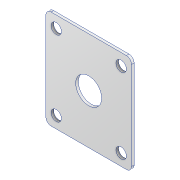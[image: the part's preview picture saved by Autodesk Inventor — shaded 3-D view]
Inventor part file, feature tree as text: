
AUTODESK INVENTOR PART (.ipt)
format: ipt  version: 2020 (Build 240168000, 168)  size: 121,344 bytes
history: native  units: mm
features: extrude x2, sketch x2, other x1, fillet x1
ambient origin geometry x8: Origin, YZ Plane, XZ Plane, XY Plane, X Axis, Y Axis, Z Axis, Center Point
bodies: Body1 (feature_tree)
feature tree (6):
  other  "솔리드1"
  extrude  "돌출1"  Depth=1.0mm TaperAngle=0.0deg
  fillet  "모깎기1"  Radius=2.0mm
  extrude  "돌출2"  Depth=10.0mm
  sketch  "스케치1"
  sketch  "스케치2"
